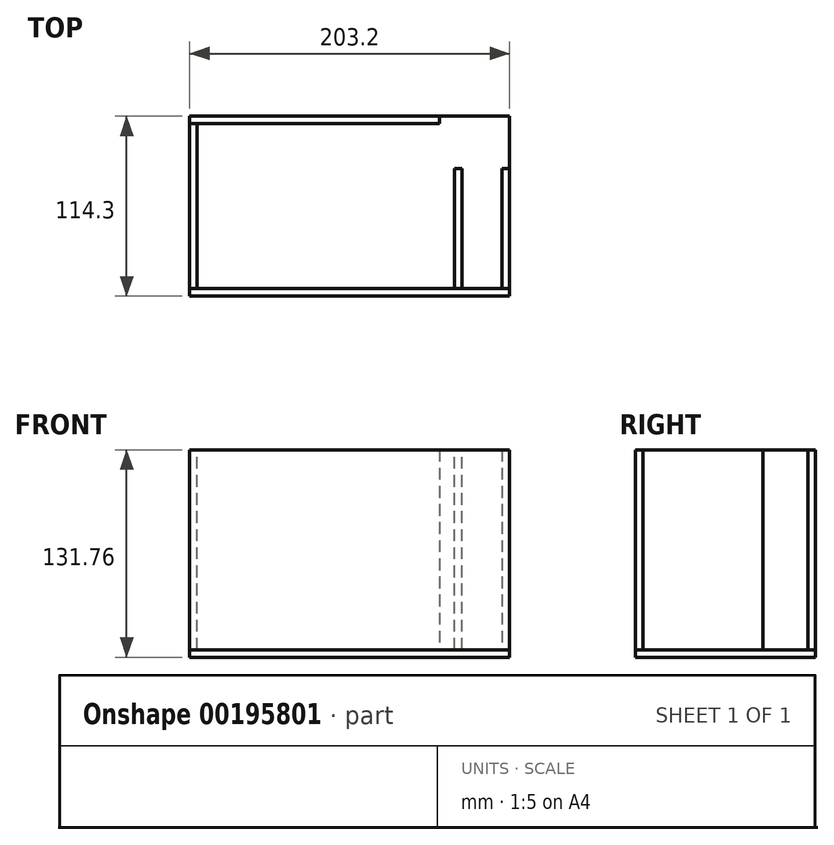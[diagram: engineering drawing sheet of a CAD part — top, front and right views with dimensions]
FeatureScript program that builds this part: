
annotation { "Feature Type Name" : "Feature", "Feature Type Description" : "" }
export const myFeature = defineFeature(function(context is Context, id is Id, definition is map)
    precondition{}
    {
        {
            var Q0;
            Q0=qCreatedBy(makeId("Top.planeOp"),FACE);
            var sketch = newSketch(context, id + "F0", { "sketchPlane" : qUnion([Q0])});
            skLineSegment(sketch, "E0", {"start": v(-203.2, 114.3) * mm, "end": v(-203.2, 0) * mm});
            skLineSegment(sketch, "E1", {"start": v(-203.2, 0) * mm, "end": v(0, 0) * mm});
            skLineSegment(sketch, "E2", {"start": v(0, 0) * mm, "end": v(0, 114.3) * mm});
            skLineSegment(sketch, "E3", {"start": v(0, 114.3) * mm, "end": v(-203.2, 114.3) * mm});
            skSolve(sketch);
        }
        {
            var Q0;
            Q0=makeQuery(id+"F0.imprint","IMPRINT",FACE,{"disambiguationData":[TD([[makeQuery(id+"F0.imprint","IMPRINT",EDGE,{"derivedFrom":sQuery(id+"F0.wireOp",EDGE,"E0")}),1.0]])]});
            extrude(context, id + "F1", {"entities" : qUnion([Q0]), "depth" : 4.76 * mm});
        }
        {
            var Q0;
            Q0=makeQuery(id+"F1.opExtrude","SWEPT_FACE",FACE,{"disambiguationData":[OSD([sQuery(id+"F0.wireOp",EDGE,"E1")])]});
            var sketch = newSketch(context, id + "F2", { "sketchPlane" : qUnion([Q0])});
            skLineSegment(sketch, "E4", {"start": v(-203.2, 4.76) * mm, "end": v(-203.2, 131.76) * mm});
            skLineSegment(sketch, "E5", {"start": v(-203.2, 131.76) * mm, "end": v(0, 131.76) * mm});
            skLineSegment(sketch, "E6", {"start": v(0, 131.76) * mm, "end": v(0, 4.76) * mm});
            skSolve(sketch);
        }
        {
            var Q0;
            Q0=makeQuery(id+"F2.imprint","IMPRINT",FACE,{"disambiguationData":[TD([[makeQuery(id+"F2.imprint","IMPRINT",EDGE,{"derivedFrom":sQuery(id+"F2.wireOp",EDGE,"E4")}),-1.0]])]});
            extrude(context, id + "F3", {"entities" : qUnion([Q0]), "oppositeDirection" : true, "depth" : 4.76 * mm});
        }
        {
            var Q0;
            Q0=makeQuery(id+"F3.opExtrude","SWEPT_FACE",FACE,{"disambiguationData":[OSD([sQuery(id+"F2.wireOp",EDGE,"E4")])]});
            var sketch = newSketch(context, id + "F4", { "sketchPlane" : qUnion([Q0])});
            skLineSegment(sketch, "E7", {"start": v(-4.76, 131.76) * mm, "end": v(-109.75, 131.76) * mm});
            skLineSegment(sketch, "E8", {"start": v(-109.75, 131.76) * mm, "end": v(-109.75, 4.76) * mm});
            skLineSegment(sketch, "E9", {"start": v(-109.75, 4.76) * mm, "end": v(-4.76, 4.76) * mm});
            skSolve(sketch);
        }
        {
            var Q0;
            Q0=makeQuery(id+"F4.imprint","IMPRINT",FACE,{"disambiguationData":[TD([[makeQuery(id+"F4.imprint","IMPRINT",EDGE,{"derivedFrom":sQuery(id+"F4.wireOp",EDGE,"E7")}),1.0]])]});
            extrude(context, id + "F5", {"entities" : qUnion([Q0]), "oppositeDirection" : true, "depth" : 4.76 * mm});
        }
        {
            var Q0;
            Q0=makeQuery(id+"F1.opExtrude","SWEPT_FACE",FACE,{"disambiguationData":[OSD([sQuery(id+"F0.wireOp",EDGE,"E3")])]});
            var sketch = newSketch(context, id + "F6", { "sketchPlane" : qUnion([Q0])});
            skLineSegment(sketch, "E10", {"start": v(203.2, 4.76) * mm, "end": v(203.2, 131.76) * mm});
            skLineSegment(sketch, "E11", {"start": v(203.2, 131.76) * mm, "end": v(44.45, 131.76) * mm});
            skLineSegment(sketch, "E12", {"start": v(44.45, 131.76) * mm, "end": v(44.45, 4.76) * mm});
            skLineSegment(sketch, "E13", {"start": v(44.45, 4.76) * mm, "end": v(203.2, 4.76) * mm});
            skSolve(sketch);
        }
        {
            var Q0;
            Q0=makeQuery(id+"F6.imprint","IMPRINT",FACE,{"disambiguationData":[TD([[makeQuery(id+"F6.imprint","IMPRINT",EDGE,{"derivedFrom":sQuery(id+"F6.wireOp",EDGE,"E10")}),1.0]])]});
            extrude(context, id + "F7", {"entities" : qUnion([Q0]), "oppositeDirection" : true, "depth" : 4.76 * mm});
        }
        {
            var Q0;
            Q0=makeQuery(id+"F1.opExtrude","SWEPT_FACE",FACE,{"disambiguationData":[OSD([sQuery(id+"F0.wireOp",EDGE,"E2")])]});
            var sketch = newSketch(context, id + "F8", { "sketchPlane" : qUnion([Q0])});
            skLineSegment(sketch, "E14.0", {"start": v(4.76, 131.76) * mm, "end": v(4.76, 4.76) * mm});
            skLineSegment(sketch, "E15", {"start": v(4.76, 131.76) * mm, "end": v(80.96, 131.76) * mm});
            skLineSegment(sketch, "E16", {"start": v(80.96, 131.76) * mm, "end": v(80.96, 4.76) * mm});
            skLineSegment(sketch, "E17", {"start": v(80.96, 4.76) * mm, "end": v(4.76, 4.76) * mm});
            skSolve(sketch);
        }
        {
            var Q0;
            Q0=makeQuery(id+"F8.imprint","IMPRINT",FACE,{"disambiguationData":[TD([[makeQuery(id+"F8.imprint","IMPRINT",EDGE,{"derivedFrom":sQuery(id+"F8.wireOp",EDGE,"E14.0")}),1.0]])]});
            extrude(context, id + "F9", {"entities" : qUnion([Q0]), "oppositeDirection" : true, "depth" : 4.76 * mm});
        }
        {
            var Q0;
            Q0=makeQuery(id+"F9.opExtrude","CAP_FACE",FACE,{"disambiguationData":[OSD([sQuery(id+"F8.wireOp",EDGE,"E14.0"),sQuery(id+"F8.wireOp",EDGE,"E15"),sQuery(id+"F8.wireOp",EDGE,"E16"),sQuery(id+"F8.wireOp",EDGE,"E17")])],"isStart":false});
            cPlane(context, id + "F10", {"entities" : qUnion([Q0]), "cplaneType" : CPlaneType.OFFSET, "offset" : 25.4 * mm, "width" : 152.4 * mm, "height" : 152.4 * mm});
        }
        {
            var Q0;
            Q0=qCreatedBy(id+"F10.planeOp",FACE);
            var sketch = newSketch(context, id + "F11", { "sketchPlane" : qUnion([Q0])});
            skLineSegment(sketch, "E18.0.0", {"start": v(-4.76, 131.76) * mm, "end": v(-80.96, 131.76) * mm});
            skLineSegment(sketch, "E18.0.1", {"start": v(-80.96, 131.76) * mm, "end": v(-80.96, 4.76) * mm});
            skLineSegment(sketch, "E18.0.2", {"start": v(-80.96, 4.76) * mm, "end": v(-4.76, 4.76) * mm});
            skLineSegment(sketch, "E18.0.3", {"start": v(-4.76, 4.76) * mm, "end": v(-4.76, 131.76) * mm});
            skSolve(sketch);
        }
        {
            var Q0;
            Q0=makeQuery(id+"F11.imprint","IMPRINT",FACE,{"disambiguationData":[TD([[makeQuery(id+"F11.imprint","IMPRINT",EDGE,{"derivedFrom":sQuery(id+"F11.wireOp",EDGE,"E18.0.0")}),1.0]])]});
            extrude(context, id + "F12", {"entities" : qUnion([Q0]), "depth" : 4.76 * mm});
        }
    });
